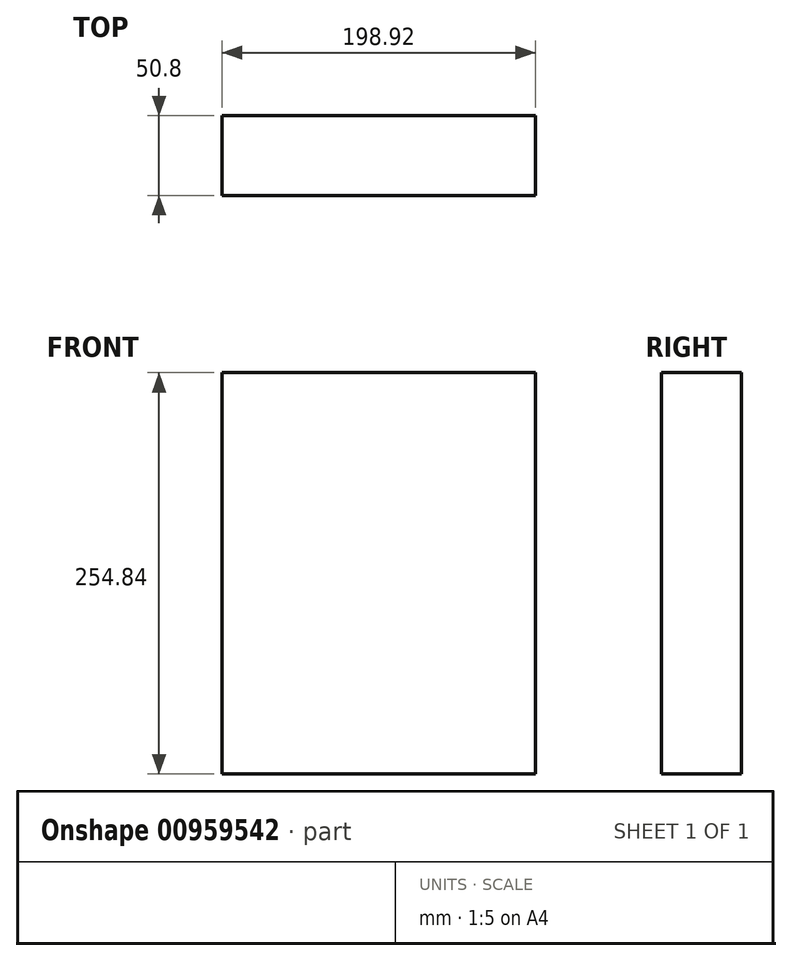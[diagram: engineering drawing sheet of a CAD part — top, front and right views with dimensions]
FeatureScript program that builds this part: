
annotation { "Feature Type Name" : "Feature", "Feature Type Description" : "" }
export const myFeature = defineFeature(function(context is Context, id is Id, definition is map)
    precondition{}
    {
        {
            var Q0;
            Q0=qCreatedBy(makeId("Front.planeOp"),FACE);
            var sketch = newSketch(context, id + "F0", { "sketchPlane" : qUnion([Q0])});
            skLineSegment(sketch, "E0.bottom", {"start": v(-99.46, 127.42) * mm, "end": v(99.46, 127.42) * mm});
            skLineSegment(sketch, "E0.top", {"start": v(-99.46, -127.42) * mm, "end": v(99.46, -127.42) * mm});
            skLineSegment(sketch, "E0.left", {"start": v(-99.46, 127.42) * mm, "end": v(-99.46, -127.42) * mm});
            skLineSegment(sketch, "E0.right", {"start": v(99.46, 127.42) * mm, "end": v(99.46, -127.42) * mm});
            skPoint(sketch, "E0.middle", {"position": v(0, 0) * mm});
            skSolve(sketch);
        }
        {
            var Q0;
            Q0=makeQuery(id+"F0.imprint","IMPRINT",FACE,{"disambiguationData":[TD([[makeQuery(id+"F0.imprint","IMPRINT",EDGE,{"derivedFrom":sQuery(id+"F0.wireOp",EDGE,"E0.bottom")}),-1.0]])]});
            extrude(context, id + "F1", {"entities" : qUnion([Q0]), "depth" : 50.8 * mm, "offsetDistance" : 25.4 * mm});
        }
    });
